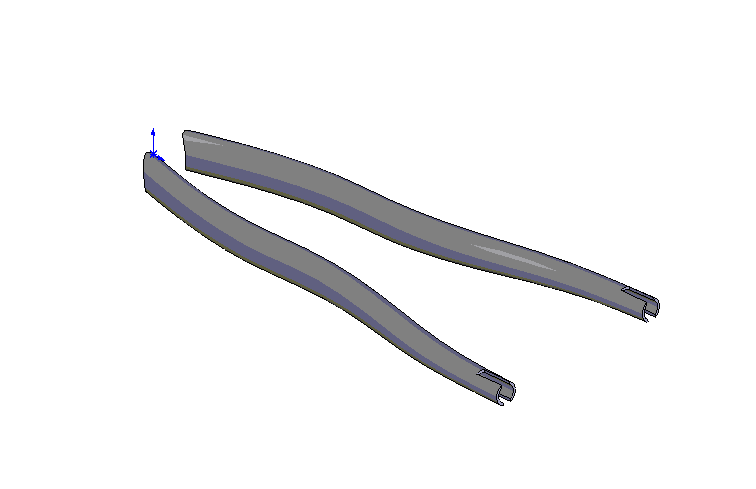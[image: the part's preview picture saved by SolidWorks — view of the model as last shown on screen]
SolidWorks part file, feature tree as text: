
SOLIDWORKS PART (.sldprt)
format: sldprt  version: not decoded by parser v0  size: 784,896 bytes
history: native  units: mm
features: plane x22, sketch x21, cut_extrude x3, shell x2, material x1 (+10 scaffold rows collapsed)
feature tree (59):
  scaffold x10  (default folders/planes/origin — collapsed)
  material  "Matériau <non spécifié>"
  plane  "Plan de face"
  plane  "Plan de dessus"
  plane  "Plan de droite"
  sketch  "Esquisse1"  dims[c1.D13=30.0mm c1.D14=14.0mm c1.D1=625.0mm c1.D2=460.0mm c1.D3=545.0mm c1.D4=27.0mm c1.D5=500.0mm c1.D6=445.0mm c1.D7=670.0mm c2.D1=622.0mm c2.D2=670.0mm c2.D3=545.0mm c2.D4=460.0mm c2.D5=445.0mm c2.D6=495.0mm c2.D7=535.0mm c2.D8=27.0mm c2.D9=8.0mm c2.D10=155.0mm c2.D11=400.0mm c2.D12=~545.374305mm c3.D12=56.0deg]
  plane  "Plan1"  Offset=71.75mm
  plane  "Plan2"  Offset=143.5mm
  plane  "Plan3"
  sketch  "Esquisse2"  dims[D9=300.0mm D10=300.0mm D11=300.0mm D1=30.0mm D2=110.0mm D3=84.0mm D4=225.0mm D5=355.0mm D6=425.0mm D7=137.0mm D8=144.0mm]
  plane  "Plan4"
  plane  "Plan5"
  plane  "Plan6"
  plane  "Plan7"
  plane  "Plan8"
  plane  "Plan9"
  plane  "Plan10"
  plane  "Plan11"
  sketch  "Esquisse3"  dims[D1=31.5mm D2=18.0mm]
  sketch  "Esquisse4"  dims[D1=18.0mm D2=31.5mm]
  sketch  "Esquisse5"  dims[D1=31.5mm D2=18.0mm]
  sketch  "Esquisse6"  dims[D1=31.5mm D2=18.0mm]
  sketch  "Esquisse7"  dims[D1=28.0mm D2=20.0mm]
  sketch  "Esquisse8"  dims[D1=22.5mm D2=20.0mm]
  sketch  "Esquisse9"  dims[D1=19.0mm D2=19.0mm]
  sketch  "Esquisse10"  dims[D1=18.0mm D2=18.0mm]
  plane  "Plan12"
  plane  "Plan13"
  plane  "Plan14"
  plane  "Plan15"
  plane  "Plan16"
  plane  "Plan17"
  plane  "Plan18"
  plane  "Plan19"
  sketch  "Esquisse11"  dims[D1=31.5mm D2=18.0mm]
  sketch  "Esquisse12"  dims[D1=31.5mm D2=18.0mm]
  sketch  "Esquisse13"  dims[D1=31.5mm D2=18.0mm]
  sketch  "Esquisse14"  dims[D1=18.0mm D2=31.5mm]
  sketch  "Esquisse15"  dims[D1=28.0mm D2=20.0mm]
  sketch  "Esquisse16"  dims[D1=22.5mm D2=20.0mm]
  sketch  "Esquisse17"  dims[D1=19.0mm D2=19.0mm]
  sketch  "Esquisse18"  dims[D1=18.0mm D2=18.0mm]
  shell  "Coque1"  Thickness=2mm
  shell  "Coque2"  Thickness=2mm
  sketch  "Esquisse19"  dims[D1=42.5mm]
  cut_extrude  "Enlèv. mat.-Extru.1"  [1 undecoded]
  sketch  "Esquisse20"  dims[D1=60.0mm]
  cut_extrude  "Enlèv. mat.-Extru.2"  Depth=7mm
  sketch  "Esquisse21"  dims[D1=~78.936758mm]
  cut_extrude  "Enlèv. mat.-Extru.3"  Depth=4.25mm
decode coverage: 25 of 26 modeling features carry decoded parameters
note: ~ marks probable driven/reference dimensions
note: 1 parameter value undecoded
note: suppression state not decoded; provenance and decode notes live in map.json
